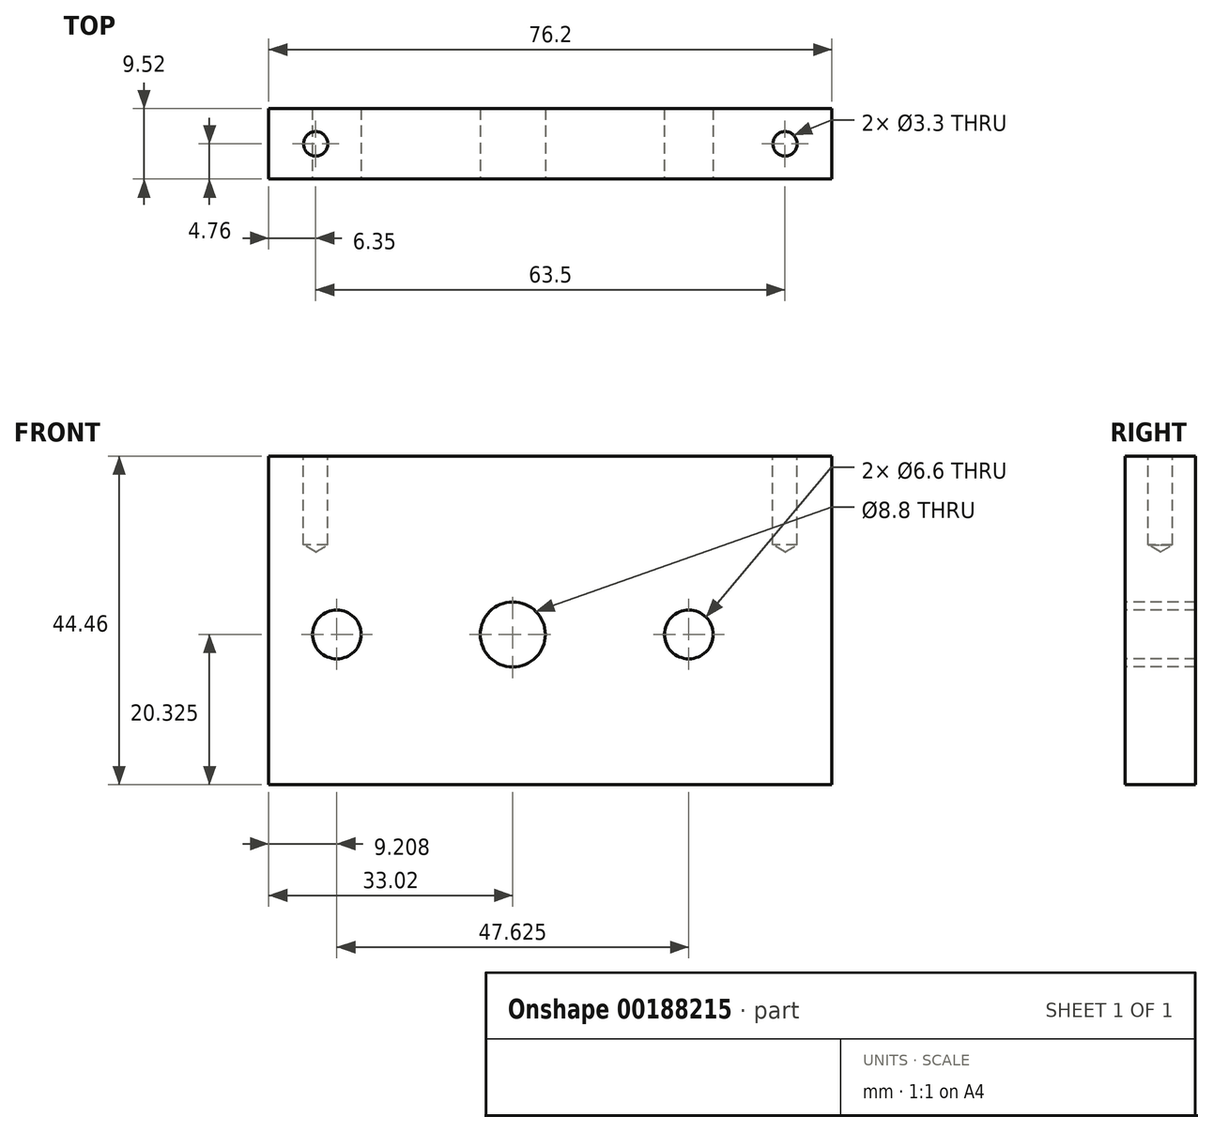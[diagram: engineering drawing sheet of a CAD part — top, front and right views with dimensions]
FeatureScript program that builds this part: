
annotation { "Feature Type Name" : "Feature", "Feature Type Description" : "" }
export const myFeature = defineFeature(function(context is Context, id is Id, definition is map)
    precondition{}
    {
        {
            var Q0;
            Q0=qCreatedBy(makeId("Front.planeOp"),FACE);
            var sketch = newSketch(context, id + "F0", { "sketchPlane" : qUnion([Q0])});
            skLineSegment(sketch, "E0.bottom", {"start": v(38.1, -22.22) * mm, "end": v(-38.1, -22.23) * mm});
            skLineSegment(sketch, "E0.top", {"start": v(38.1, 22.23) * mm, "end": v(-38.1, 22.22) * mm});
            skLineSegment(sketch, "E0.left", {"start": v(38.1, -22.23) * mm, "end": v(38.1, 22.23) * mm});
            skLineSegment(sketch, "E0.right", {"start": v(-38.1, -22.23) * mm, "end": v(-38.1, 22.22) * mm});
            skPoint(sketch, "E0.middle", {"position": v(0, 0) * mm});
            skSolve(sketch);
        }
        {
            var Q0;
            Q0=qSketchRegion(id+"F0",true);
            extrude(context, id + "F1", {"entities" : qUnion([Q0]), "endBound" : BoundingType.SYMMETRIC, "depth" : 9.52 * mm});
        }
        {
            var Q0;
            Q0=makeQuery(id+"F1.opExtrude","SWEPT_FACE",FACE,{"disambiguationData":[OSD([sQuery(id+"F0.wireOp",EDGE,"E0.top")])]});
            var sketch = newSketch(context, id + "F2", { "sketchPlane" : qUnion([Q0])});
            skPoint(sketch, "E1", {"position": v(-31.75, 0) * mm});
            skPoint(sketch, "E2.1.0.0", {"position": v(31.75, 0) * mm});
            skLineSegment(sketch, "E2.direction1", {"start": v(-31.75, 0) * mm, "end": v(31.75, 0) * mm, "construction": true});
            skSolve(sketch);
        }
        {
            var Q0;
            Q0=sQuery(id+"F2.wireOp",VERTEX,"E1");
            var Q1;
            Q1=sQuery(id+"F2.wireOp",VERTEX,"E2.1.0.0");
            var Q2;
            Q2=makeQuery(id+"F1.opExtrude","SWEPT_BODY",BODY,{"disambiguationData":[OSD([sQuery(id+"F0.wireOp",EDGE,"E0.bottom"),sQuery(id+"F0.wireOp",EDGE,"E0.top"),sQuery(id+"F0.wireOp",EDGE,"E0.left"),sQuery(id+"F0.wireOp",EDGE,"E0.right")])]});
            hole(context, id + "F3", {"style" : HoleStyle.SIMPLE, "endStyle" : HoleEndStyle.BLIND, "standardTappedOrClearance" : lookupTablePath({ "standard" : "ISO", "engagement" : "75%", "pitch" : "0.7 mm", "size" : "M4", "type" : "Tapped" }), "standardBlindInLast" : lookupTablePath({ "standard" : "ISO", "engagement" : "75%", "pitch" : "0.7 mm", "size" : "M4", "type" : "Tapped" }), "holeDiameter" : 3.3 * mm, "holeDepth" : 12 * mm, "startFromSketch" : true, "locations" : qUnion([Q0, Q1]), "scope" : qUnion([Q2]), "majorDiameter" : 4 * mm});
        }
        {
            var Q0;
            Q0=makeQuery(id+"F1.opExtrude","CAP_FACE",FACE,{"disambiguationData":[OSD([sQuery(id+"F0.wireOp",EDGE,"E0.bottom"),sQuery(id+"F0.wireOp",EDGE,"E0.top"),sQuery(id+"F0.wireOp",EDGE,"E0.left"),sQuery(id+"F0.wireOp",EDGE,"E0.right")])],"isStart":false});
            var sketch = newSketch(context, id + "F4", { "sketchPlane" : qUnion([Q0])});
            skPoint(sketch, "E3", {"position": v(-28.9, -1.9) * mm});
            skPoint(sketch, "E4", {"position": v(18.73, -1.9) * mm});
            skSolve(sketch);
        }
        {
            var Q0;
            Q0=sQuery(id+"F4.wireOp",VERTEX,"E3");
            var Q1;
            Q1=sQuery(id+"F4.wireOp",VERTEX,"E4");
            var Q2;
            Q2=makeQuery(id+"F1.opExtrude","SWEPT_BODY",BODY,{"disambiguationData":[OSD([sQuery(id+"F0.wireOp",EDGE,"E0.bottom"),sQuery(id+"F0.wireOp",EDGE,"E0.top"),sQuery(id+"F0.wireOp",EDGE,"E0.left"),sQuery(id+"F0.wireOp",EDGE,"E0.right")])]});
            hole(context, id + "F5", {"style" : HoleStyle.SIMPLE, "endStyle" : HoleEndStyle.BLIND, "standardTappedOrClearance" : lookupTablePath({ "standard" : "ISO", "fit" : "Normal", "size" : "M6", "type" : "Clearance" }), "standardBlindInLast" : lookupTablePath({ "fit" : "Standard", "standard" : "ISO", "size" : "M6", "type" : "Clearance" }), "holeDiameter" : 6.6 * mm, "holeDepth" : 12.7 * mm, "startFromSketch" : true, "locations" : qUnion([Q0, Q1]), "scope" : qUnion([Q2])});
        }
        {
            var Q0;
            Q0=makeQuery(id+"F1.opExtrude","CAP_FACE",FACE,{"disambiguationData":[OSD([sQuery(id+"F0.wireOp",EDGE,"E0.bottom"),sQuery(id+"F0.wireOp",EDGE,"E0.top"),sQuery(id+"F0.wireOp",EDGE,"E0.left"),sQuery(id+"F0.wireOp",EDGE,"E0.right")])],"isStart":false});
            var sketch = newSketch(context, id + "F6", { "sketchPlane" : qUnion([Q0])});
            skPoint(sketch, "E5", {"position": v(-5.08, -1.9) * mm});
            skSolve(sketch);
        }
        {
            var Q0;
            Q0=sQuery(id+"F6.wireOp",VERTEX,"E5");
            var Q1;
            Q1=makeQuery(id+"F1.opExtrude","SWEPT_BODY",BODY,{"disambiguationData":[OSD([sQuery(id+"F0.wireOp",EDGE,"E0.bottom"),sQuery(id+"F0.wireOp",EDGE,"E0.top"),sQuery(id+"F0.wireOp",EDGE,"E0.left"),sQuery(id+"F0.wireOp",EDGE,"E0.right")])]});
            hole(context, id + "F7", {"style" : HoleStyle.SIMPLE, "endStyle" : HoleEndStyle.THROUGH, "standardTappedOrClearance" : lookupTablePath({ "standard" : "ISO", "fit" : "Normal", "size" : "M8", "type" : "Clearance" }), "standardBlindInLast" : lookupTablePath({ "fit" : "Standard", "standard" : "ISO", "size" : "M8", "type" : "Clearance" }), "holeDiameter" : 8.8 * mm, "startFromSketch" : true, "locations" : qUnion([Q0]), "scope" : qUnion([Q1]), "isTappedThrough" : true});
        }
    });
